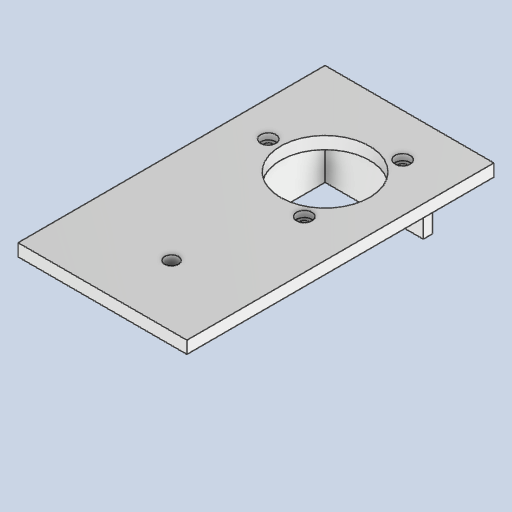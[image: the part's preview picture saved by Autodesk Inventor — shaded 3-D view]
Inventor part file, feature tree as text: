
AUTODESK INVENTOR PART (.ipt)
format: ipt  version: 2023 (Build 270158000, 158)  size: 267,776 bytes
history: native  units: in
note: dims shown in document units (in); Inventor stores cm internally (conversion verified against a paired STEP export)
features: other x6, extrude x5, sketch x5
ambient origin geometry x8: Origin, YZ Plane, XZ Plane, XY Plane, X Axis, Y Axis, Z Axis, Center Point
bodies: Body1 (feature_tree), Body2 (feature_tree)
feature tree (16):
  other  "GIM3505-8_with-driver.ipt"
  other  "ソリッド1"
  extrude  "押し出し1"  Depth=0.3937in
  extrude  "押し出し2"  Depth=1.1811in
  sketch  "スケッチ3"
  other  "作業平面1"
  sketch  "スケッチ6"
  extrude  "押し出し7"  Depth=0.9843in
  extrude  "押し出し8"  Depth=1.1811in
  extrude  "押し出し9"  Depth=3.937in
  other  "TaggingFeature1"
  sketch  "スケッチ1"
  sketch  "スケッチ2"
  sketch  "スケッチ7"
  other  "ソリッド1::GIM3505-8_with-driver.ipt"
  other  "Srf1"
